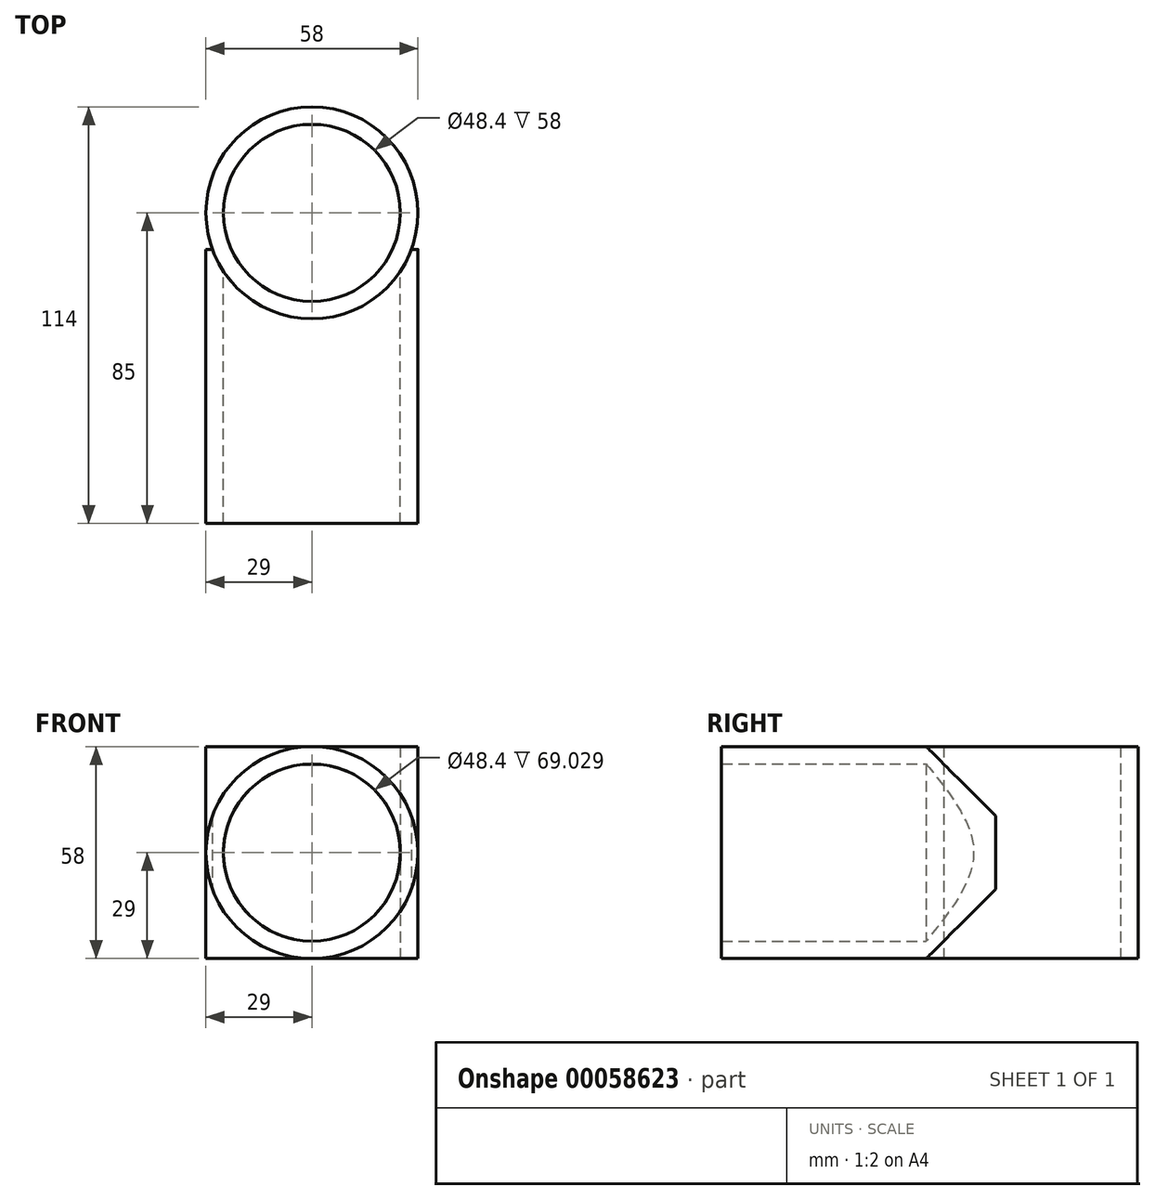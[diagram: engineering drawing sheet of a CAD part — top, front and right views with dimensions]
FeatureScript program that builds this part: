
annotation { "Feature Type Name" : "Feature", "Feature Type Description" : "" }
export const myFeature = defineFeature(function(context is Context, id is Id, definition is map)
    precondition{}
    {
        {
            var Q0;
            Q0=qCreatedBy(makeId("Front.planeOp"),FACE);
            var sketch = newSketch(context, id + "F0", { "sketchPlane" : qUnion([Q0])});
            skCircle(sketch, "E0", {"center": v(0, 0) * mm, "radius": 29 * mm});
            skCircle(sketch, "E1", {"center": v(0, 0) * mm, "radius": 24.2 * mm});
            skSolve(sketch);
        }
        {
            var Q0;
            Q0=makeQuery(id+"F0.imprint","IMPRINT",FACE,{"disambiguationData":[TD([[makeQuery(id+"F0.imprint","IMPRINT",EDGE,{"derivedFrom":sQuery(id+"F0.wireOp",EDGE,"E0")}),1.0]])]});
            extrude(context, id + "F1", {"entities" : qUnion([Q0]), "depth" : 75 * mm});
        }
        {
            var Q0;
            Q0=qCreatedBy(makeId("Top.planeOp"),FACE);
            var sketch = newSketch(context, id + "F2", { "sketchPlane" : qUnion([Q0])});
            skCircle(sketch, "E2", {"center": v(0, 10) * mm, "radius": 24.2 * mm});
            skCircle(sketch, "E3", {"center": v(0, 10) * mm, "radius": 29 * mm});
            skSolve(sketch);
        }
        {
            var Q0;
            Q0 = qSketchRegion(id + "F2", true);
            extrude(context, id + "F3", {"entities" : qUnion([Q0]), "operationType" : NewBodyOperationType.ADD, "depth" : 29 * mm, "hasSecondDirection" : true, "secondDirectionOppositeDirection" : true, "secondDirectionDepth" : 29 * mm});
        }
        {
            var Q0;
            Q0=makeQuery(id+"F3.opExtrude","CAP_FACE",FACE,{"disambiguationData":[OSD([sQuery(id+"F2.wireOp",EDGE,"E2"),sQuery(id+"F2.wireOp",EDGE,"E3")])],"isStart":false});
            var sketch = newSketch(context, id + "F4", { "sketchPlane" : qUnion([Q0])});
            skCircle(sketch, "E4", {"center": v(0, 10) * mm, "radius": 24.2 * mm});
            skSolve(sketch);
        }
        {
            var Q0;
            Q0 = qSketchRegion(id + "F4", true);
            extrude(context, id + "F5", {"entities" : qUnion([Q0]), "operationType" : NewBodyOperationType.REMOVE, "endBound" : BoundingType.THROUGH_ALL, "oppositeDirection" : true, "depth" : 25 * mm});
        }
    });
